# Revit family: Drinking_Fountain-Haws_Corporation-Pedestal_3670
name_source: partatom
category: Plumbing Fixtures
revit_build: Autodesk Revit 2015 (Build: 20140606_1530(x64)
units: mm (PartAtom-declared; Revit-internal decimal feet)

## types (1)
- 3670
    BIMobject category = Taps & Mixers
    BIMobject category code = sanitary-taps-mixers
    BIMobject main category = Sanitary
    BIMobject main category code = sanitary
    Brand url = https://www.hawsco.com
    Default Elevation = 48"
    Description = Modular Outdoor Bottle Filler Dog Bowl

Double click to view larger
Zoom Out
Zoom In

Modular Outdoor Bottle Filler Dog Bowl
    Design country = United States
    Edition number = 1
    Flow Rate = 1.0 GPM
    Installation instructions = https://www.hawsco.com
    Manufacturer = Haws Corporation
    Manufacturer country = United States
    Manufacturer name = Haws Corporation
    Masterformat 2014 Code = 22 47 13
    Masterformat 2014 Description = Drinking Fountains
    Material main = Metal
    Material_chrome = Metal - Haws Corporation - Polished Chrome - 5703M
    Material_inserts = Acetal Resin-Haws Corporation- Black
    Model = 3670
    Nominal height = 9"
    Nominal width = 10"
    OmniClass Code = 23-31 31 00
    OmniClass Description = Drinking Fountains
    Pedestal = Metal - Haws Corporation - Green Powder Coated Finish
    Product Guid = 0d775c96-7ae9-427b-a106-2f7d3194a9ff
    Product SKU = haws-3670
    Product data url = https://bimobject.com
    Product family = Drinking Fountains/Coolers
    Product group = Pedestal Mounted Drinking Fountains
    Product url = https://www.hawsco.com
    QR code = http://bimobject.com
    Technical description = https://www.hawsco.com
    URL = www.hawsco.com/
    Uniclass 1.4 Code = L7213
    Uniclass 1.4 Description = Fountains
    Uniclass 2.0 Code = SS-35-65-70-25
    Uniclass 2.0 Description = Drinking Fountain Systems
    Uniclass 2015 Code = Pr_40_20_87_24
    Uniclass 2015 Name = Drinking fountains
    Weight Net (Kg) = 0

## geometry (parser evidence)
native form markers: Sweep x6
no freeform markers — native parametric forms only
